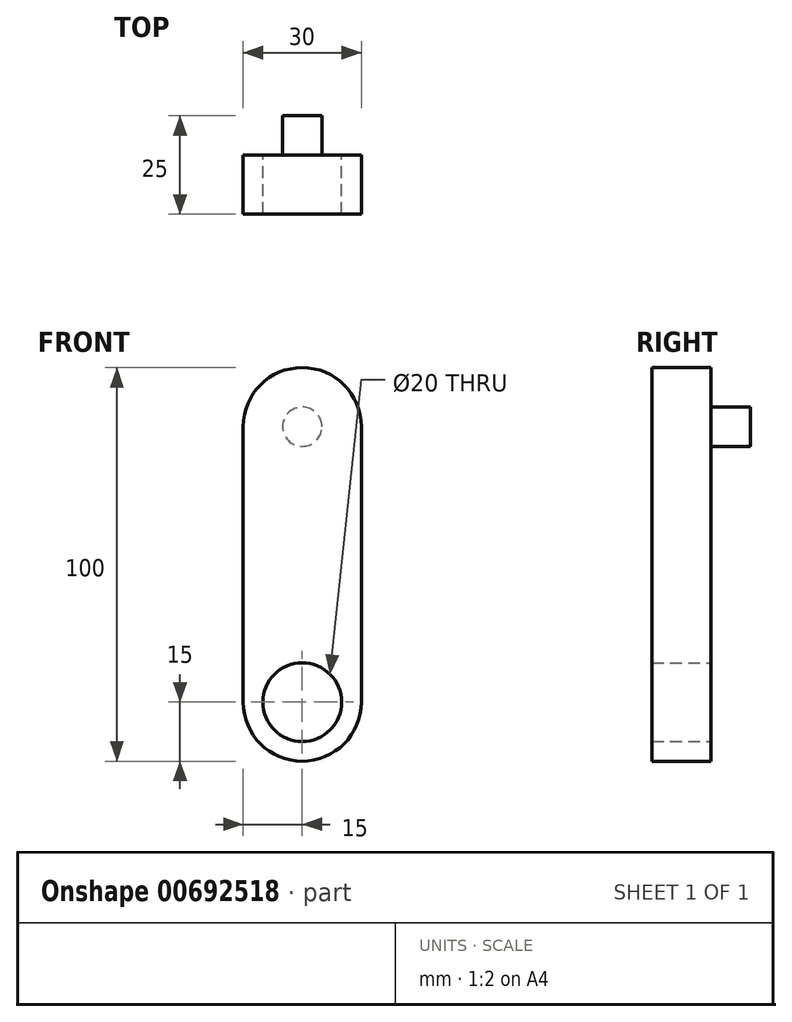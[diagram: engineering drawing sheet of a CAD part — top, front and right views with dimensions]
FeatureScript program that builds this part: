
annotation { "Feature Type Name" : "Feature", "Feature Type Description" : "" }
export const myFeature = defineFeature(function(context is Context, id is Id, definition is map)
    precondition{}
    {
        {
            var Q0;
            Q0=qCreatedBy(makeId("Front.planeOp"),FACE);
            var sketch = newSketch(context, id + "F0", { "sketchPlane" : qUnion([Q0])});
            skLineSegment(sketch, "E0.bottom", {"start": v(0, -50) * mm, "end": v(0, -50) * mm});
            skLineSegment(sketch, "E0.top", {"start": v(0, 50) * mm, "end": v(0, 50) * mm});
            skLineSegment(sketch, "E0.left", {"start": v(15, -35) * mm, "end": v(15, 35) * mm});
            skLineSegment(sketch, "E0.right", {"start": v(-15, -35) * mm, "end": v(-15, 35) * mm});
            skPoint(sketch, "E0.middle", {"position": v(0, 0) * mm});
            skPoint(sketch, "E1.visualSharp", {"position": v(-15, 50) * mm});
            skArc(sketch, "E1.filletArc", {"start": v(0, 50) * mm, "mid": v(-10.6, 45.6) * mm, "end": v(-15, 35) * mm});
            skPoint(sketch, "E2.visualSharp", {"position": v(15, 50) * mm});
            skArc(sketch, "E2.filletArc", {"start": v(15, 35) * mm, "mid": v(10.6, 45.6) * mm, "end": v(0, 50) * mm});
            skPoint(sketch, "E3.visualSharp", {"position": v(15, -50) * mm});
            skArc(sketch, "E3.filletArc", {"start": v(0, -50) * mm, "mid": v(10.6, -45.6) * mm, "end": v(15, -35) * mm});
            skPoint(sketch, "E4.visualSharp", {"position": v(-15, -50) * mm});
            skArc(sketch, "E4.filletArc", {"start": v(-15, -35) * mm, "mid": v(-10.6, -45.6) * mm, "end": v(0, -50) * mm});
            skCircle(sketch, "E5", {"center": v(0, -35) * mm, "radius": 10 * mm});
            skSolve(sketch);
        }
        {
            var Q0;
            Q0=makeQuery(id+"F0.imprint","IMPRINT",FACE,{"disambiguationData":[TD([[makeQuery(id+"F0.imprint","IMPRINT",EDGE,{"derivedFrom":sQuery(id+"F0.wireOp",EDGE,"E0.left")}),1.0]])]});
            extrude(context, id + "F1", {"entities" : qUnion([Q0]), "depth" : 15 * mm, "offsetDistance" : 25 * mm});
        }
        {
            var Q0;
            Q0=qCreatedBy(makeId("Front.planeOp"),FACE);
            var sketch = newSketch(context, id + "F2", { "sketchPlane" : qUnion([Q0])});
            skArc(sketch, "E6.0", {"start": v(15, 35) * mm, "mid": v(0, 50) * mm, "end": v(-15, 35) * mm});
            skLineSegment(sketch, "E7", {"start": v(0, 50) * mm, "end": v(0, 35) * mm});
            skCircle(sketch, "E8", {"center": v(0, 35) * mm, "radius": 5 * mm});
            skSolve(sketch);
        }
        {
            var Q0;
            Q0=makeQuery(id+"F2.imprint","IMPRINT",FACE,{"disambiguationData":[TD([[makeQuery(id+"F2.imprint","IMPRINT",EDGE,{"derivedFrom":sQuery(id+"F2.wireOp",EDGE,"E8")}),1.0]])]});
            extrude(context, id + "F3", {"entities" : qUnion([Q0]), "operationType" : NewBodyOperationType.ADD, "oppositeDirection" : true, "depth" : 10 * mm, "offsetDistance" : 25 * mm});
        }
    });
